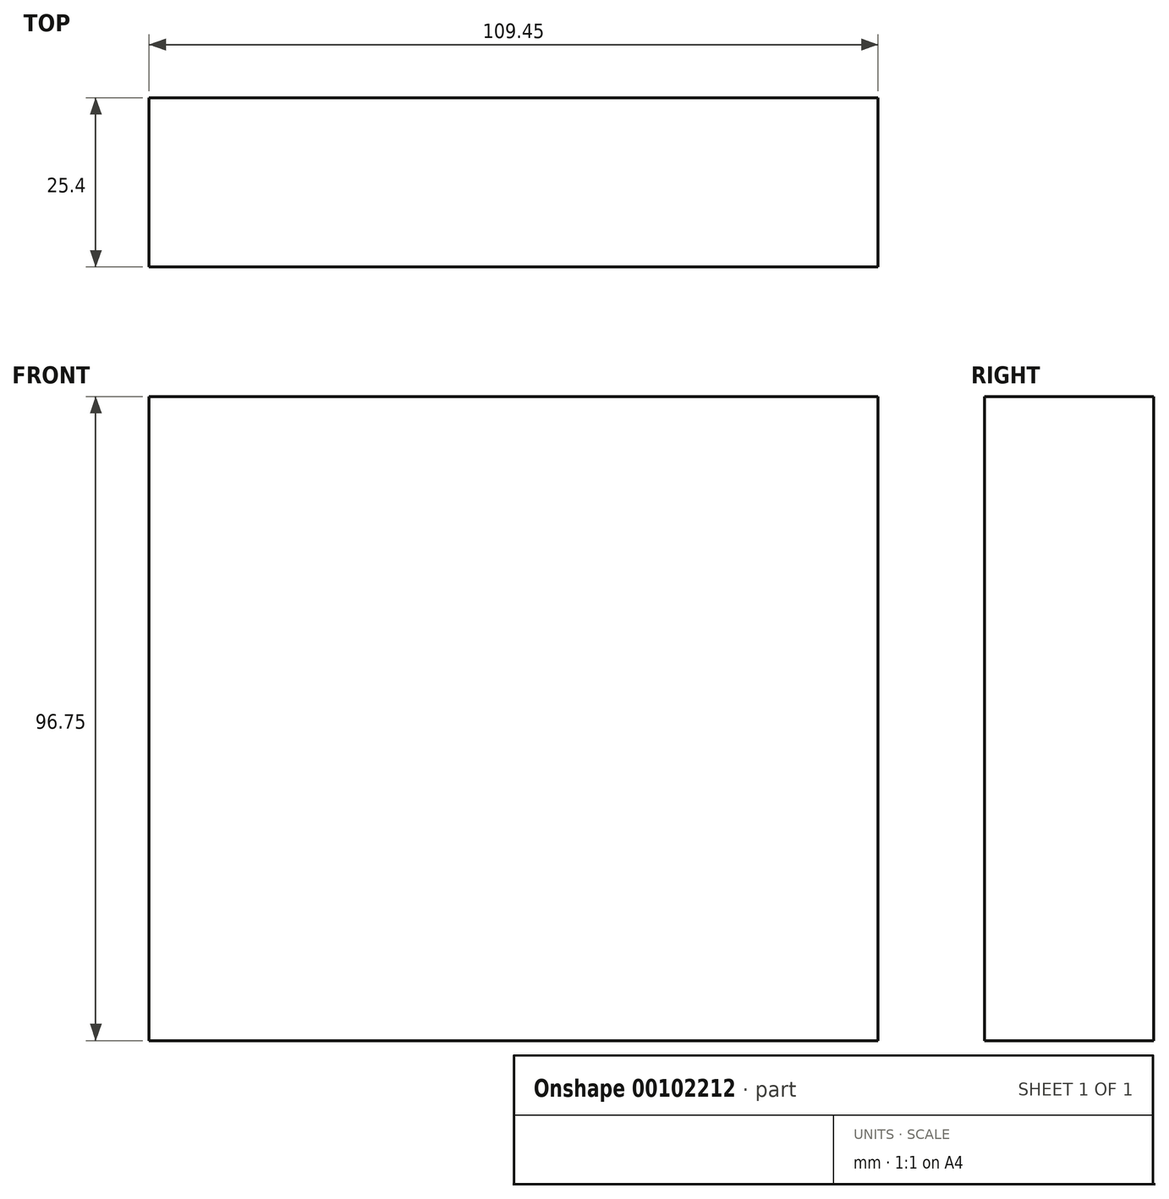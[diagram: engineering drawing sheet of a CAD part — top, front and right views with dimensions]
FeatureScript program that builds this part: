
annotation { "Feature Type Name" : "Feature", "Feature Type Description" : "" }
export const myFeature = defineFeature(function(context is Context, id is Id, definition is map)
    precondition{}
    {
        {
            var Q0;
            Q0=qCreatedBy(makeId("Front.planeOp"),FACE);
            var sketch = newSketch(context, id + "F0", { "sketchPlane" : qUnion([Q0])});
            skLineSegment(sketch, "E0.bottom", {"start": v(-53.1, 49.53) * mm, "end": v(56.34, 49.53) * mm});
            skLineSegment(sketch, "E0.top", {"start": v(-53.1, -47.22) * mm, "end": v(56.34, -47.22) * mm});
            skLineSegment(sketch, "E0.left", {"start": v(-53.1, 49.53) * mm, "end": v(-53.1, -47.22) * mm});
            skLineSegment(sketch, "E0.right", {"start": v(56.34, 49.53) * mm, "end": v(56.34, -47.22) * mm});
            skSolve(sketch);
        }
        {
            var Q0;
            Q0 = qSketchRegion(id + "F0", true);
            extrude(context, id + "F1", {"entities" : qUnion([Q0]), "depth" : 25.4 * mm});
        }
    });
